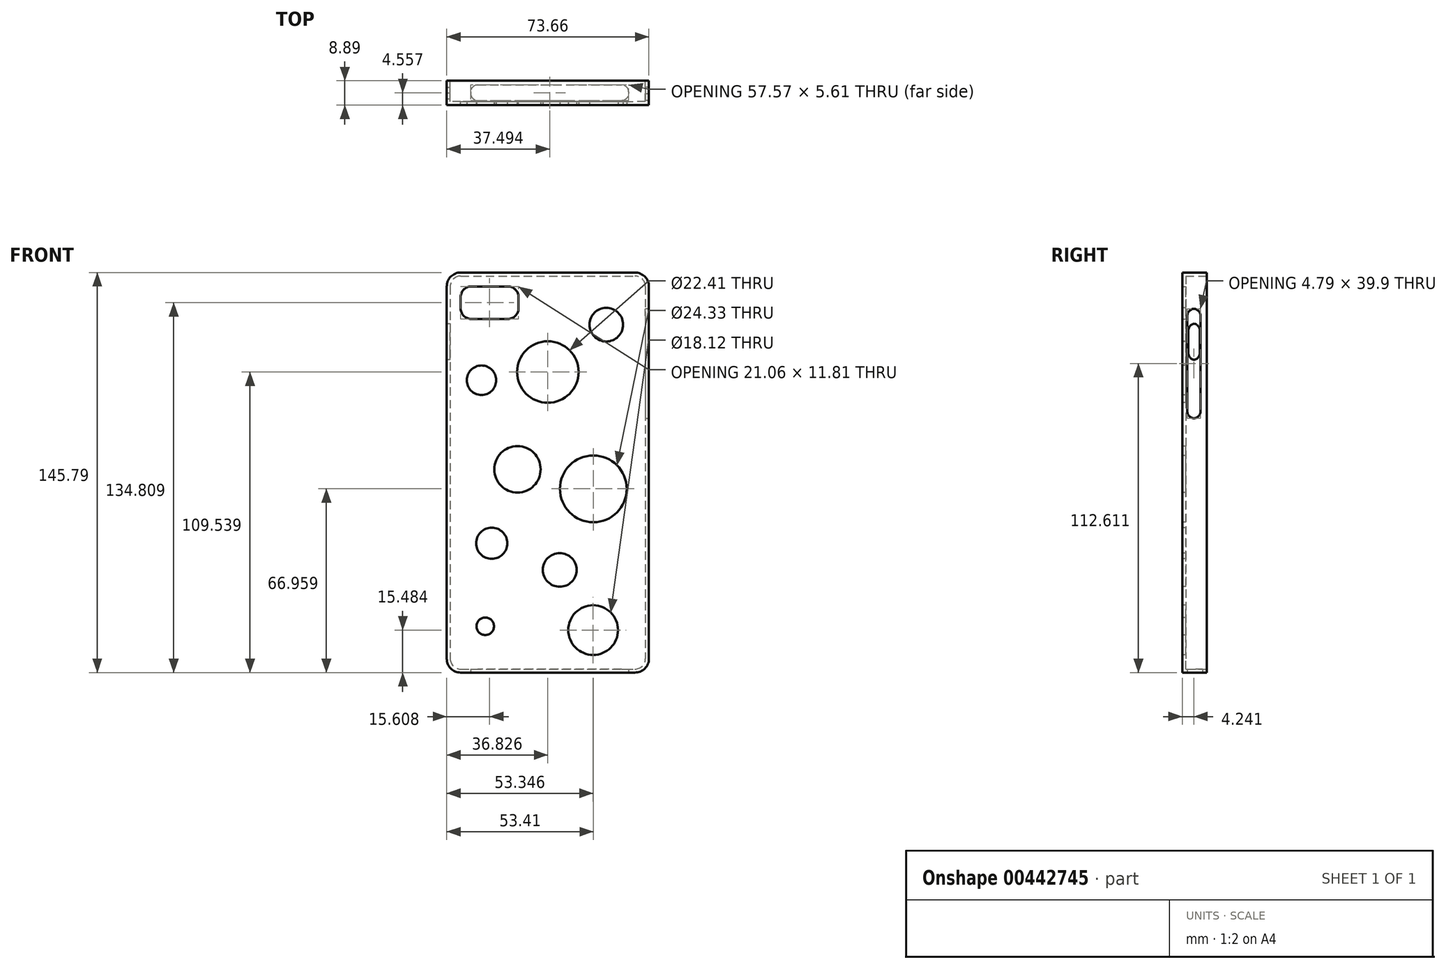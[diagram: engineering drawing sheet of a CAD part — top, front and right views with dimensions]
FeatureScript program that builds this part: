
annotation { "Feature Type Name" : "Feature", "Feature Type Description" : "" }
export const myFeature = defineFeature(function(context is Context, id is Id, definition is map)
    precondition{}
    {
        {
            var Q0;
            Q0=qCreatedBy(makeId("Front.planeOp"),FACE);
            var sketch = newSketch(context, id + "F0", { "sketchPlane" : qUnion([Q0])});
            skLineSegment(sketch, "E0", {"start": v(-42.6, 55.8) * mm, "end": v(-42.6, -90) * mm});
            skLineSegment(sketch, "E1", {"start": v(-42.6, 55.8) * mm, "end": v(31.07, 55.8) * mm});
            skLineSegment(sketch, "E2", {"start": v(31.07, 55.8) * mm, "end": v(31.07, -90) * mm});
            skLineSegment(sketch, "E3", {"start": v(-42.6, -90) * mm, "end": v(31.07, -90) * mm});
            skSolve(sketch);
        }
        {
            var Q0;
            Q0 = qSketchRegion(id + "F0", true);
            extrude(context, id + "F1", {"entities" : qUnion([Q0]), "depth" : 8.9 * mm});
        }
        {
            var Q0;
            Q0=makeQuery(id+"F1.opExtrude","SWEPT_EDGE",EDGE,{"disambiguationData":[OSD([sQuery(id+"F0.wireOp",EDGE,"E1"),sQuery(id+"F0.wireOp",EDGE,"E2")])]});
            var Q1;
            Q1=makeQuery(id+"F1.opExtrude","SWEPT_EDGE",EDGE,{"disambiguationData":[OSD([sQuery(id+"F0.wireOp",EDGE,"E0"),sQuery(id+"F0.wireOp",EDGE,"E1")])]});
            var Q2;
            Q2=makeQuery(id+"F1.opExtrude","SWEPT_EDGE",EDGE,{"disambiguationData":[OSD([sQuery(id+"F0.wireOp",EDGE,"E2"),sQuery(id+"F0.wireOp",EDGE,"E3")])]});
            var Q3;
            Q3=makeQuery(id+"F1.opExtrude","SWEPT_EDGE",EDGE,{"disambiguationData":[OSD([sQuery(id+"F0.wireOp",EDGE,"E0"),sQuery(id+"F0.wireOp",EDGE,"E3")])]});
            fillet(context, id + "F2", {"entities" : qUnion([Q0, Q1, Q2, Q3]), "radius" : 5.08 * mm, "tangentPropagation" : true, "allowEdgeOverflow" : false});
        }
        {
            var Q0;
            Q0=makeQuery(id+"F1.opExtrude","CAP_FACE",FACE,{"disambiguationData":[OSD([sQuery(id+"F0.wireOp",EDGE,"E0"),sQuery(id+"F0.wireOp",EDGE,"E1"),sQuery(id+"F0.wireOp",EDGE,"E2"),sQuery(id+"F0.wireOp",EDGE,"E3")])],"isStart":false});
            var sketch = newSketch(context, id + "F3", { "sketchPlane" : qUnion([Q0])});
            skLineSegment(sketch, "E4.bottom", {"start": v(-37.51, 50.72) * mm, "end": v(-16.45, 50.72) * mm});
            skLineSegment(sketch, "E4.top", {"start": v(-37.51, 38.92) * mm, "end": v(-16.45, 38.92) * mm});
            skLineSegment(sketch, "E4.left", {"start": v(-37.51, 50.72) * mm, "end": v(-37.51, 38.92) * mm});
            skLineSegment(sketch, "E4.right", {"start": v(-16.45, 50.72) * mm, "end": v(-16.45, 38.92) * mm});
            skSolve(sketch);
        }
        {
            var Q0;
            Q0=makeQuery(id+"F3.imprint","IMPRINT",FACE,{"disambiguationData":[TD([[makeQuery(id+"F3.imprint","IMPRINT",EDGE,{"derivedFrom":sQuery(id+"F3.wireOp",EDGE,"E4.bottom")}),-1.0]])]});
            extrude(context, id + "F4", {"entities" : qUnion([Q0]), "operationType" : NewBodyOperationType.REMOVE, "endBound" : BoundingType.SYMMETRIC, "depth" : 25.4 * mm});
        }
        {
            var Q0;
            Q0=makeQuery(id+"F4.boolean.opBoolean","COPY",EDGE,{"derivedFrom":makeQuery(id+"F4.opExtrude","SWEPT_EDGE",EDGE,{"disambiguationData":[OSD([sQuery(id+"F3.wireOp",EDGE,"E4.bottom"),sQuery(id+"F3.wireOp",EDGE,"E4.right")])]})});
            var Q1;
            Q1=makeQuery(id+"F4.boolean.opBoolean","COPY",EDGE,{"derivedFrom":makeQuery(id+"F4.opExtrude","SWEPT_EDGE",EDGE,{"disambiguationData":[OSD([sQuery(id+"F3.wireOp",EDGE,"E4.bottom"),sQuery(id+"F3.wireOp",EDGE,"E4.left")])]})});
            var Q2;
            Q2=makeQuery(id+"F4.boolean.opBoolean","COPY",EDGE,{"derivedFrom":makeQuery(id+"F4.opExtrude","SWEPT_EDGE",EDGE,{"disambiguationData":[OSD([sQuery(id+"F3.wireOp",EDGE,"E4.top"),sQuery(id+"F3.wireOp",EDGE,"E4.left")])]})});
            var Q3;
            Q3=makeQuery(id+"F4.boolean.opBoolean","COPY",EDGE,{"derivedFrom":makeQuery(id+"F4.opExtrude","SWEPT_EDGE",EDGE,{"disambiguationData":[OSD([sQuery(id+"F3.wireOp",EDGE,"E4.top"),sQuery(id+"F3.wireOp",EDGE,"E4.right")])]})});
            fillet(context, id + "F5", {"entities" : qUnion([Q0, Q1, Q2, Q3]), "radius" : 3.8 * mm, "tangentPropagation" : true, "allowEdgeOverflow" : false});
        }
        {
            var Q0;
            Q0=makeQuery(id+"F1.opExtrude","CAP_FACE",FACE,{"disambiguationData":[OSD([sQuery(id+"F0.wireOp",EDGE,"E0"),sQuery(id+"F0.wireOp",EDGE,"E1"),sQuery(id+"F0.wireOp",EDGE,"E2"),sQuery(id+"F0.wireOp",EDGE,"E3")])],"isStart":true});
            var sketch = newSketch(context, id + "F6", { "sketchPlane" : qUnion([Q0])});
            skSolve(sketch);
        }
        {
            var Q0;
            Q0=makeQuery(id+"F1.opExtrude","CAP_FACE",FACE,{"disambiguationData":[OSD([sQuery(id+"F0.wireOp",EDGE,"E0"),sQuery(id+"F0.wireOp",EDGE,"E1"),sQuery(id+"F0.wireOp",EDGE,"E2"),sQuery(id+"F0.wireOp",EDGE,"E3")])],"isStart":true});
            shell(context, id + "F7", {"entities" : qUnion([Q0]), "thickness" : 1.27 * mm});
        }
        {
            var Q0;
            {var subQ3=sQuery(id+"F0.wireOp",EDGE,"E0");Q0=makeQuery(id+"F6.imprint","IMPRINT",FACE,{"disambiguationData":[TD([[makeQuery(id+"F6.imprint","IMPRINT",EDGE,{"derivedFrom":makeQuery(id+"F1.opExtrude","CAP_EDGE",EDGE,{"disambiguationData":[OSD([subQ3])],"isStart":true})}),-1.0]])]});}
            var sketch = newSketch(context, id + "F8", { "sketchPlane" : qUnion([Q0])});
            skLineSegment(sketch, "E5", {"start": v(11.24, 51.83) * mm, "end": v(11.24, 31.84) * mm});
            skLineSegment(sketch, "E6", {"start": v(11.24, 31.84) * mm, "end": v(37.27, 33.5) * mm});
            skLineSegment(sketch, "E7", {"start": v(37.27, 33.5) * mm, "end": v(40.13, 42.72) * mm});
            skLineSegment(sketch, "E8", {"start": v(40.13, 42.72) * mm, "end": v(38.73, 52.09) * mm});
            skLineSegment(sketch, "E9", {"start": v(38.73, 52.09) * mm, "end": v(23.24, 53.49) * mm});
            skLineSegment(sketch, "E10", {"start": v(23.24, 53.49) * mm, "end": v(11.24, 51.83) * mm});
            skSolve(sketch);
        }
        {
            var Q0;
            Q0 = qSketchRegion(id + "F8", true);
            extrude(context, id + "F9", {"entities" : qUnion([Q0]), "operationType" : NewBodyOperationType.REMOVE, "oppositeDirection" : true, "depth" : 7.62 * mm});
        }
        {
            var Q0;
            Q0=makeQuery(id+"F1.opExtrude","SWEPT_FACE",FACE,{"disambiguationData":[OSD([sQuery(id+"F0.wireOp",EDGE,"E0")])]});
            var sketch = newSketch(context, id + "F10", { "sketchPlane" : qUnion([Q0])});
            skLineSegment(sketch, "E11.bottom", {"start": v(2.5, 37.25) * mm, "end": v(6.66, 37.25) * mm});
            skLineSegment(sketch, "E11.top", {"start": v(2.5, 23.92) * mm, "end": v(6.66, 23.92) * mm});
            skLineSegment(sketch, "E11.left", {"start": v(2.5, 37.25) * mm, "end": v(2.5, 23.92) * mm});
            skLineSegment(sketch, "E11.right", {"start": v(6.66, 37.25) * mm, "end": v(6.66, 23.92) * mm});
            skSolve(sketch);
        }
        {
            var Q0;
            Q0 = qSketchRegion(id + "F10", true);
            extrude(context, id + "F11", {"entities" : qUnion([Q0]), "operationType" : NewBodyOperationType.REMOVE, "oppositeDirection" : true, "depth" : 25.4 * mm});
        }
        {
            var Q0;
            Q0=makeQuery(id+"F11.boolean.opBoolean","COPY",EDGE,{"derivedFrom":makeQuery(id+"F11.opExtrude","SWEPT_EDGE",EDGE,{"disambiguationData":[OSD([sQuery(id+"F10.wireOp",EDGE,"E11.bottom"),sQuery(id+"F10.wireOp",EDGE,"E11.right")])]})});
            var Q1;
            Q1=makeQuery(id+"F11.boolean.opBoolean","COPY",EDGE,{"derivedFrom":makeQuery(id+"F11.opExtrude","SWEPT_EDGE",EDGE,{"disambiguationData":[OSD([sQuery(id+"F10.wireOp",EDGE,"E11.top"),sQuery(id+"F10.wireOp",EDGE,"E11.right")])]})});
            var Q2;
            Q2=makeQuery(id+"F11.boolean.opBoolean","COPY",EDGE,{"derivedFrom":makeQuery(id+"F11.opExtrude","SWEPT_EDGE",EDGE,{"disambiguationData":[OSD([sQuery(id+"F10.wireOp",EDGE,"E11.bottom"),sQuery(id+"F10.wireOp",EDGE,"E11.left")])]})});
            var Q3;
            Q3=makeQuery(id+"F11.boolean.opBoolean","COPY",EDGE,{"derivedFrom":makeQuery(id+"F11.opExtrude","SWEPT_EDGE",EDGE,{"disambiguationData":[OSD([sQuery(id+"F10.wireOp",EDGE,"E11.top"),sQuery(id+"F10.wireOp",EDGE,"E11.left")])]})});
            fillet(context, id + "F12", {"entities" : qUnion([Q0, Q1, Q2, Q3]), "radius" : 2.54 * mm, "tangentPropagation" : true, "allowEdgeOverflow" : false});
        }
        {
            var Q0;
            Q0=makeQuery(id+"F1.opExtrude","SWEPT_FACE",FACE,{"disambiguationData":[OSD([sQuery(id+"F0.wireOp",EDGE,"E3")])]});
            var sketch = newSketch(context, id + "F13", { "sketchPlane" : qUnion([Q0])});
            skLineSegment(sketch, "E12.bottom", {"start": v(-33.88, 1.53) * mm, "end": v(23.69, 1.53) * mm});
            skLineSegment(sketch, "E12.top", {"start": v(-33.88, 7.14) * mm, "end": v(23.69, 7.14) * mm});
            skLineSegment(sketch, "E12.left", {"start": v(-33.88, 1.53) * mm, "end": v(-33.88, 7.14) * mm});
            skLineSegment(sketch, "E12.right", {"start": v(23.69, 1.53) * mm, "end": v(23.69, 7.14) * mm});
            skSolve(sketch);
        }
        {
            var Q0;
            Q0 = qSketchRegion(id + "F13", true);
            extrude(context, id + "F14", {"entities" : qUnion([Q0]), "operationType" : NewBodyOperationType.REMOVE, "oppositeDirection" : true, "depth" : 25.4 * mm});
        }
        {
            var Q0;
            Q0=makeQuery(id+"F14.boolean.opBoolean","COPY",EDGE,{"derivedFrom":makeQuery(id+"F14.opExtrude","SWEPT_EDGE",EDGE,{"disambiguationData":[OSD([sQuery(id+"F13.wireOp",EDGE,"E12.top"),sQuery(id+"F13.wireOp",EDGE,"E12.left")])]})});
            var Q1;
            Q1=makeQuery(id+"F14.boolean.opBoolean","COPY",EDGE,{"derivedFrom":makeQuery(id+"F14.opExtrude","SWEPT_EDGE",EDGE,{"disambiguationData":[OSD([sQuery(id+"F13.wireOp",EDGE,"E12.top"),sQuery(id+"F13.wireOp",EDGE,"E12.right")])]})});
            var Q2;
            Q2=makeQuery(id+"F14.boolean.opBoolean","COPY",EDGE,{"derivedFrom":makeQuery(id+"F14.opExtrude","SWEPT_EDGE",EDGE,{"disambiguationData":[OSD([sQuery(id+"F13.wireOp",EDGE,"E12.bottom"),sQuery(id+"F13.wireOp",EDGE,"E12.left")])]})});
            var Q3;
            Q3=makeQuery(id+"F14.boolean.opBoolean","COPY",EDGE,{"derivedFrom":makeQuery(id+"F14.opExtrude","SWEPT_EDGE",EDGE,{"disambiguationData":[OSD([sQuery(id+"F13.wireOp",EDGE,"E12.bottom"),sQuery(id+"F13.wireOp",EDGE,"E12.right")])]})});
            fillet(context, id + "F15", {"entities" : qUnion([Q0, Q1, Q2, Q3]), "radius" : 2.54 * mm, "tangentPropagation" : true, "allowEdgeOverflow" : false});
        }
        {
            var Q0;
            Q0=makeQuery(id+"F1.opExtrude","SWEPT_FACE",FACE,{"disambiguationData":[OSD([sQuery(id+"F0.wireOp",EDGE,"E2")])]});
            var sketch = newSketch(context, id + "F16", { "sketchPlane" : qUnion([Q0])});
            skLineSegment(sketch, "E13.bottom", {"start": v(-7.05, 42.57) * mm, "end": v(-2.25, 42.57) * mm});
            skLineSegment(sketch, "E13.top", {"start": v(-7.05, 2.67) * mm, "end": v(-2.25, 2.67) * mm});
            skLineSegment(sketch, "E13.left", {"start": v(-7.05, 42.57) * mm, "end": v(-7.05, 2.67) * mm});
            skLineSegment(sketch, "E13.right", {"start": v(-2.25, 42.57) * mm, "end": v(-2.25, 2.67) * mm});
            skSolve(sketch);
        }
        {
            var Q0;
            Q0=makeQuery(id+"F16.imprint","IMPRINT",FACE,{"disambiguationData":[TD([[makeQuery(id+"F16.imprint","IMPRINT",EDGE,{"derivedFrom":sQuery(id+"F16.wireOp",EDGE,"E13.bottom")}),-1.0]])]});
            extrude(context, id + "F17", {"entities" : qUnion([Q0]), "operationType" : NewBodyOperationType.REMOVE, "oppositeDirection" : true, "depth" : 25.4 * mm});
        }
        {
            var Q0;
            Q0=makeQuery(id+"F17.boolean.opBoolean","COPY",EDGE,{"derivedFrom":makeQuery(id+"F17.opExtrude","SWEPT_EDGE",EDGE,{"disambiguationData":[OSD([sQuery(id+"F16.wireOp",EDGE,"E13.bottom"),sQuery(id+"F16.wireOp",EDGE,"E13.right")])]})});
            var Q1;
            Q1=makeQuery(id+"F17.boolean.opBoolean","COPY",EDGE,{"derivedFrom":makeQuery(id+"F17.opExtrude","SWEPT_EDGE",EDGE,{"disambiguationData":[OSD([sQuery(id+"F16.wireOp",EDGE,"E13.top"),sQuery(id+"F16.wireOp",EDGE,"E13.right")])]})});
            var Q2;
            Q2=makeQuery(id+"F17.boolean.opBoolean","COPY",EDGE,{"derivedFrom":makeQuery(id+"F17.opExtrude","SWEPT_EDGE",EDGE,{"disambiguationData":[OSD([sQuery(id+"F16.wireOp",EDGE,"E13.bottom"),sQuery(id+"F16.wireOp",EDGE,"E13.left")])]})});
            var Q3;
            Q3=makeQuery(id+"F17.boolean.opBoolean","COPY",EDGE,{"derivedFrom":makeQuery(id+"F17.opExtrude","SWEPT_EDGE",EDGE,{"disambiguationData":[OSD([sQuery(id+"F16.wireOp",EDGE,"E13.top"),sQuery(id+"F16.wireOp",EDGE,"E13.left")])]})});
            fillet(context, id + "F18", {"entities" : qUnion([Q0, Q1, Q2, Q3]), "radius" : 2.54 * mm, "tangentPropagation" : true, "allowEdgeOverflow" : false});
        }
        {
            var Q0;
            Q0=makeQuery(id+"F1.opExtrude","CAP_FACE",FACE,{"disambiguationData":[OSD([sQuery(id+"F0.wireOp",EDGE,"E0"),sQuery(id+"F0.wireOp",EDGE,"E1"),sQuery(id+"F0.wireOp",EDGE,"E2"),sQuery(id+"F0.wireOp",EDGE,"E3")])],"isStart":false});
            var sketch = newSketch(context, id + "F19", { "sketchPlane" : qUnion([Q0])});
            skLineSegment(sketch, "E14", {"start": v(-5.76, 55.8) * mm, "end": v(-5.76, -55) * mm});
            skCircle(sketch, "E15", {"center": v(-5.76, 19.55) * mm, "radius": 11.2 * mm});
            skSolve(sketch);
        }
        {
            var Q0;
            {var subQ0=sQuery(id+"F19.wireOp",EDGE,"E15");var subQ1=sQuery(id+"F19.wireOp",EDGE,"E14");var subQ2=makeQuery(id+"F19.imprint","INTERSECT",VERTEX,{"disambiguationData":[OD(0.0)],"derivedFrom":[subQ1,subQ0]});Q0=makeQuery(id+"F19.imprint","IMPRINT",FACE,{"disambiguationData":[TD([[makeQuery(id+"F19.imprint","IMPRINT",EDGE,{"disambiguationData":[TD([[subQ2,1.0]])],"derivedFrom":subQ1}),-1.0]])]});}
            var Q1;
            {var subQ0=sQuery(id+"F19.wireOp",EDGE,"E15");var subQ1=sQuery(id+"F19.wireOp",EDGE,"E14");var subQ2=makeQuery(id+"F19.imprint","INTERSECT",VERTEX,{"disambiguationData":[OD(0.0)],"derivedFrom":[subQ1,subQ0]});Q1=makeQuery(id+"F19.imprint","IMPRINT",FACE,{"disambiguationData":[TD([[makeQuery(id+"F19.imprint","IMPRINT",EDGE,{"disambiguationData":[TD([[subQ2,1.0]])],"derivedFrom":subQ1}),1.0]])]});}
            extrude(context, id + "F20", {"entities" : qUnion([Q0, Q1]), "operationType" : NewBodyOperationType.REMOVE, "oppositeDirection" : true, "depth" : 25.4 * mm});
        }
        {
            var Q0;
            Q0=makeQuery(id+"F1.opExtrude","CAP_FACE",FACE,{"disambiguationData":[OSD([sQuery(id+"F0.wireOp",EDGE,"E0"),sQuery(id+"F0.wireOp",EDGE,"E1"),sQuery(id+"F0.wireOp",EDGE,"E2"),sQuery(id+"F0.wireOp",EDGE,"E3")])],"isStart":false});
            var sketch = newSketch(context, id + "F21", { "sketchPlane" : qUnion([Q0])});
            skCircle(sketch, "E16", {"center": v(-26.21, -42.87) * mm, "radius": 5.68 * mm});
            skCircle(sketch, "E17", {"center": v(10.82, -23.03) * mm, "radius": 12.16 * mm});
            skCircle(sketch, "E18", {"center": v(10.76, -74.5) * mm, "radius": 9.06 * mm});
            skCircle(sketch, "E19", {"center": v(-16.81, -15.92) * mm, "radius": 8.44 * mm});
            skCircle(sketch, "E20", {"center": v(-1.42, -52.59) * mm, "radius": 6.13 * mm});
            skCircle(sketch, "E21", {"center": v(-29.93, 16.55) * mm, "radius": 5.37 * mm});
            skCircle(sketch, "E22", {"center": v(15.54, 36.8) * mm, "radius": 6.14 * mm});
            skCircle(sketch, "E23", {"center": v(-28.56, -73.12) * mm, "radius": 3.18 * mm});
            skSolve(sketch);
        }
        {
            var Q0;
            Q0=makeQuery(id+"F21.imprint","IMPRINT",FACE,{"disambiguationData":[TD([[makeQuery(id+"F21.imprint","IMPRINT",EDGE,{"derivedFrom":sQuery(id+"F21.wireOp",EDGE,"E17")}),1.0]])]});
            var Q1;
            Q1=makeQuery(id+"F21.imprint","IMPRINT",FACE,{"disambiguationData":[TD([[makeQuery(id+"F21.imprint","IMPRINT",EDGE,{"derivedFrom":sQuery(id+"F21.wireOp",EDGE,"E19")}),1.0]])]});
            var Q2;
            Q2=makeQuery(id+"F21.imprint","IMPRINT",FACE,{"disambiguationData":[TD([[makeQuery(id+"F21.imprint","IMPRINT",EDGE,{"derivedFrom":sQuery(id+"F21.wireOp",EDGE,"E16")}),1.0]])]});
            var Q3;
            Q3=makeQuery(id+"F21.imprint","IMPRINT",FACE,{"disambiguationData":[TD([[makeQuery(id+"F21.imprint","IMPRINT",EDGE,{"derivedFrom":sQuery(id+"F21.wireOp",EDGE,"E20")}),1.0]])]});
            var Q4;
            Q4=makeQuery(id+"F21.imprint","IMPRINT",FACE,{"disambiguationData":[TD([[makeQuery(id+"F21.imprint","IMPRINT",EDGE,{"derivedFrom":sQuery(id+"F21.wireOp",EDGE,"E18")}),1.0]])]});
            var Q5;
            Q5=makeQuery(id+"F21.imprint","IMPRINT",FACE,{"disambiguationData":[TD([[makeQuery(id+"F21.imprint","IMPRINT",EDGE,{"derivedFrom":sQuery(id+"F21.wireOp",EDGE,"E23")}),1.0]])]});
            var Q6;
            Q6=makeQuery(id+"F21.imprint","IMPRINT",FACE,{"disambiguationData":[TD([[makeQuery(id+"F21.imprint","IMPRINT",EDGE,{"derivedFrom":sQuery(id+"F21.wireOp",EDGE,"E21")}),1.0]])]});
            var Q7;
            Q7=makeQuery(id+"F21.imprint","IMPRINT",FACE,{"disambiguationData":[TD([[makeQuery(id+"F21.imprint","IMPRINT",EDGE,{"derivedFrom":sQuery(id+"F21.wireOp",EDGE,"E22")}),1.0]])]});
            extrude(context, id + "F22", {"entities" : qUnion([Q0, Q1, Q2, Q3, Q4, Q5, Q6, Q7]), "operationType" : NewBodyOperationType.REMOVE, "oppositeDirection" : true, "depth" : 25.4 * mm});
        }
    });
